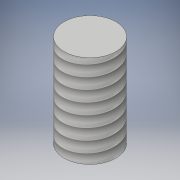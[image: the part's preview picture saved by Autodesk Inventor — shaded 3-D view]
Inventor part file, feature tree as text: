
AUTODESK INVENTOR PART (.ipt)
format: ipt  version: 2017 (Build 210142000, 142)  size: 103,424 bytes
history: native  units: in
note: dims shown in document units (in); Inventor stores cm internally (conversion verified against a paired STEP export)
features: extrude x1, thread x1, sketch x1
ambient origin geometry x8: Origin, YZ Plane, XZ Plane, XY Plane, X Axis, Y Axis, Z Axis, Center Point
bodies: Body1 (feature_tree)
feature tree (3):
  extrude  "Extrusion4"  Depth=0.35in TaperAngle=0.0deg
  thread  "Thread2"  [1 undecoded]
  sketch  "Sketch5"  dims[d11=0.196in d12=0.35in d13=0.0in d14=1.0in d15=0.0in]
note: 1 required parameter value undecoded (feature->parameter linkage not recoverable at this tier; creation-order binding heuristic only, values carry confidence <= 0.55)
